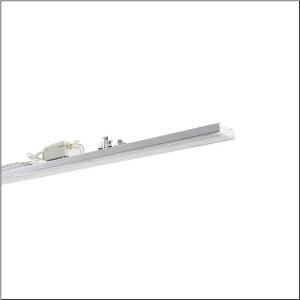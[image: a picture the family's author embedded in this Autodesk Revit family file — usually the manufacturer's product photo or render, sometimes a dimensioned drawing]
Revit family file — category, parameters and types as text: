
# Revit family: licross_r__21_recessed_ho_52tl12dv4lxm_44ad
name_source: partatom
category: Lighting Fixtures
units: mm (PartAtom-declared; Revit-internal decimal feet)

## family parameters
Cut with Voids When Loaded = No
Host = Face
Light Source = No
Part Type = Normal
Room Calculation Point = No
Round Connector Dimension = Use Diameter
Shared = No

## types (1)
- --- (1 x LED, 20000 lm, 109.8 W, 4000K)
    Apparent Load = 110 VA
    CIE Flux Codes = 69 91 98 100 100
    Color Rendering = 80
    Color Temperature = 4000K
    Default Elevation = 1800 mm
    Description = Licross® 21 Recessed HO, luminaire insert, of sheet steel, galvanised, coil coated, white, length: 2.250mm, width: 66mm, height: 67mm, LED rated luminous flux: 20.000lm, light colour: 840, control gear: DALI 2, with plug, 5-pole, with phase selection, mains connection: 220..240V, AC, 50/60Hz, rated input power: 110W, halogen-free wiring, primary optical cover: cover, of PMMA, light emission: direct distribution, primary light characteristic: symmetric, protection rating (complete): IP40, insulation class (complete): insulation class I (protective earthing), certification: CE, ENEC, VDE, UKCA, protection symbol: D if used in an environment without relevant dust loads with corresponding accessories, impact resistance: IK06, permissible ambient temperature for indoor applications: -40..+35°C, corresponds to IFS (International Featured Standards) requirements for safety and quality in the food industry, reducing of maximum allowable ambient temperature of 5°C with ceiling mounting, LABS conformity tested according to VDMA 24364:2018-05, packaging unit: 1 piece
    Height = 58 mm
    Lamp = 1 x LED
    Lamp Light Flux = 20000 lm
    Lamp Power = 109.8 W
    Lamp count = 1
    Length = 2250 mm
    Luminous efficacy = 182 lm/W
    Manufacturer = Siteco
    ModVariant = No
    Model = 52TL12DV4LXM
    Mounting Place = Ceiling
    Mounting Type = Pendant
    Number of Poles = 1
    OnlyDefault = Yes
    Power Factor = 1
    Product Name = Licross® 21 Recessed HO
    Product group = luminaire insert
    ProductGroupID = 901
    Protection Class = Protection class I
    Protection Degree = IP 40
    RLX_Detail_Level = 1
    RLX_Emergency_Light_Flux = 0 lm
    RLX_Emergency_Type = 0
    RLX_Emergency_Type_DB = No
    RlxData = <blob elided: 29501 chars, md5=3837b202>
    Socket = socket
    Standby Power = 0 W
    System Light Flux = 20000 lm
    System Power = 110 W
    Type Comments = factory setting: luminous flux: 100 % | dim-lin: 254 | 425 mA
    Type Image = l_1296930.jpg
    URL = http://relux.com
    VarID = @adj_046723
    Voltage = 0 V
    Weight = 0.00 kg
    Width = 66 mm

## geometry (parser evidence)
native form markers: Blend x4, Sweep x10
no freeform markers — native parametric forms only
